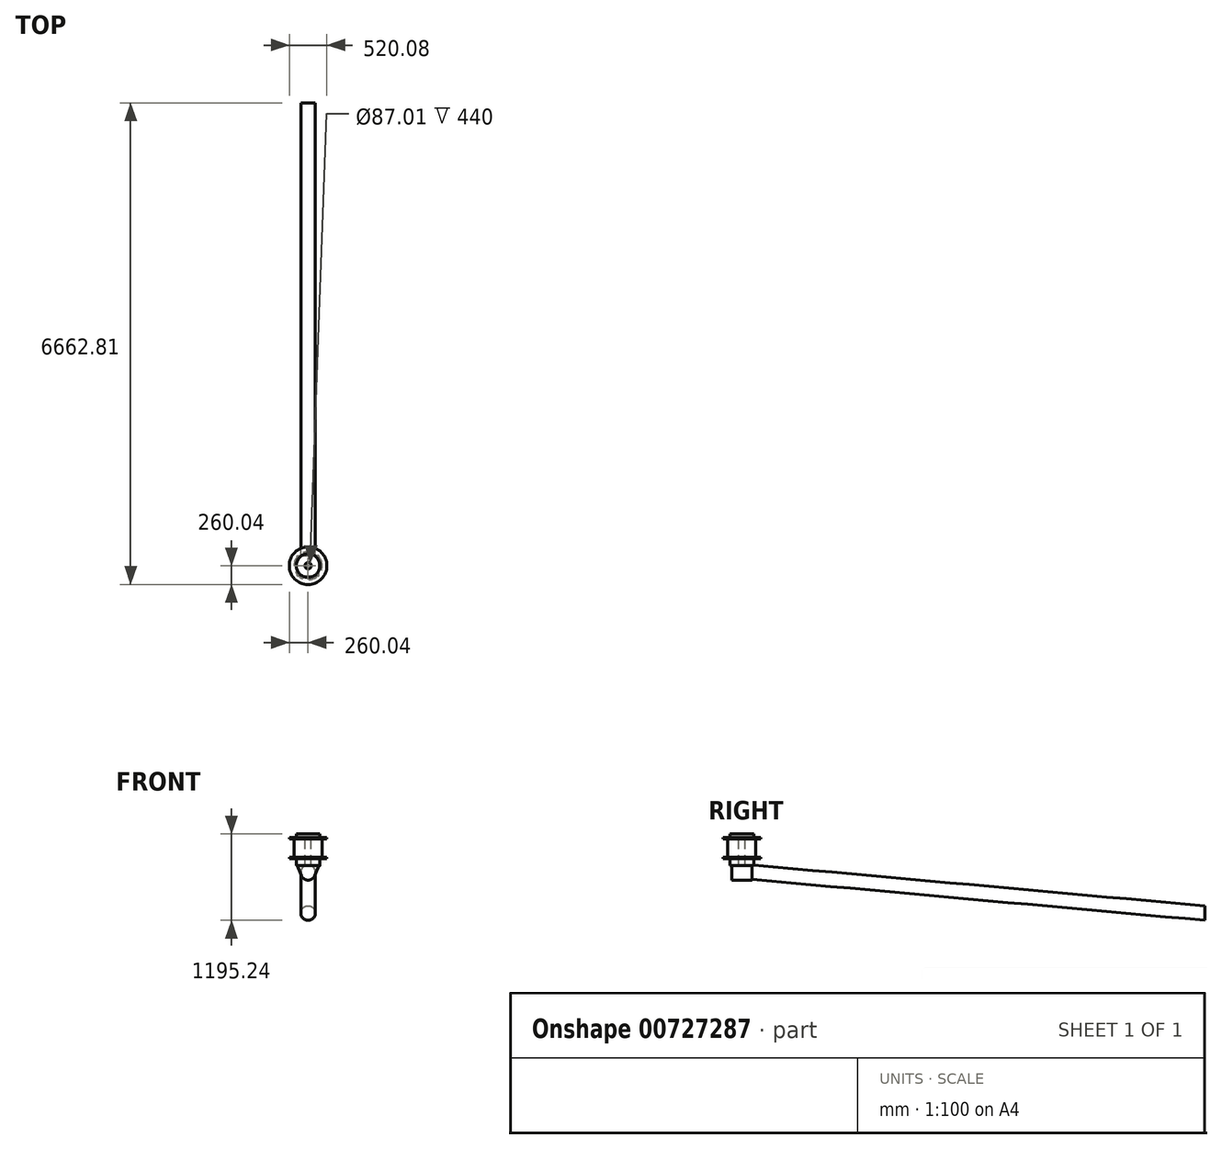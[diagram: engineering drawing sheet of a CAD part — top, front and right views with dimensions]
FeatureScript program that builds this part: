
annotation { "Feature Type Name" : "Feature", "Feature Type Description" : "" }
export const myFeature = defineFeature(function(context is Context, id is Id, definition is map)
    precondition{}
    {
        {
            var Q0;
            Q0=qCreatedBy(makeId("Front.planeOp"),FACE);
            var sketch = newSketch(context, id + "F0", { "sketchPlane" : qUnion([Q0])});
            skLineSegment(sketch, "E0", {"start": v(0, 326.34) * mm, "end": v(0, -233.1) * mm, "construction": true});
            skLineSegment(sketch, "E1", {"start": v(-43.5, 342.85) * mm, "end": v(-163.5, 342.85) * mm});
            skLineSegment(sketch, "E2", {"start": v(-163.5, 342.85) * mm, "end": v(-163.5, 292.85) * mm});
            skLineSegment(sketch, "E3", {"start": v(-163.5, 292.85) * mm, "end": v(-260.04, 292.85) * mm});
            skLineSegment(sketch, "E4", {"start": v(-260.04, 292.85) * mm, "end": v(-260.04, 272.85) * mm});
            skLineSegment(sketch, "E5", {"start": v(-260.04, 272.85) * mm, "end": v(-193.5, 272.85) * mm});
            skLineSegment(sketch, "E6", {"start": v(-193.5, 272.85) * mm, "end": v(-193.5, 22.85) * mm});
            skLineSegment(sketch, "E7", {"start": v(-193.5, 22.85) * mm, "end": v(-260.04, 22.85) * mm});
            skLineSegment(sketch, "E8", {"start": v(-260.04, 22.85) * mm, "end": v(-260.04, 2.85) * mm});
            skLineSegment(sketch, "E9", {"start": v(-260.04, 2.85) * mm, "end": v(-163.5, 2.85) * mm});
            skLineSegment(sketch, "E10", {"start": v(-163.5, 2.85) * mm, "end": v(-163.5, -97.15) * mm});
            skLineSegment(sketch, "E11", {"start": v(-163.5, -97.15) * mm, "end": v(-43.5, -97.15) * mm});
            skLineSegment(sketch, "E12", {"start": v(-43.5, -97.15) * mm, "end": v(-43.5, 342.85) * mm});
            skSolve(sketch);
        }
        {
            var Q0;
            Q0 = qSketchRegion(id + "F0", true);
            var Q1;
            Q1=sQuery(id+"F0.wireOp",EDGE,"E0");
            revolve(context, id + "F1", {"surfaceOperationType" : NewSurfaceOperationType.NEW, "entities" : qUnion([Q0]), "axis" : qUnion([Q1]), "revolveType" : RevolveType.FULL});
        }
        {
            var Q0;
            Q0=qCreatedBy(makeId("Front.planeOp"),FACE);
            var sketch = newSketch(context, id + "F2", { "sketchPlane" : qUnion([Q0])});
            skArc(sketch, "E13", {"start": v(-93.15, -233.51) * mm, "mid": v(0, -297.15) * mm, "end": v(93.15, -233.51) * mm});
            skLineSegment(sketch, "E14", {"start": v(-146.38, -97.15) * mm, "end": v(-93.15, -233.51) * mm});
            skLineSegment(sketch, "E15", {"start": v(146.38, -97.15) * mm, "end": v(93.15, -233.51) * mm});
            skLineSegment(sketch, "E16", {"start": v(-146.38, -97.15) * mm, "end": v(146.38, -97.15) * mm});
            skSolve(sketch);
        }
        {
            var Q0;
            Q0 = qSketchRegion(id + "F2", true);
            extrude(context, id + "F3", {"entities" : qUnion([Q0]), "operationType" : NewBodyOperationType.ADD, "endBound" : BoundingType.SYMMETRIC, "depth" : 277.37 * mm, "offsetDistance" : 25.4 * mm});
        }
        {
            var Q0;
            Q0=qCreatedBy(makeId("Right.planeOp"),FACE);
            cPlane(context, id + "F4", {"entities" : qUnion([Q0]), "cplaneType" : CPlaneType.OFFSET, "offset" : 0 * mm, "width" : 152.4 * mm, "height" : 152.4 * mm});
        }
        {
            var Q0;
            Q0=qCreatedBy(id+"F4.planeOp",FACE);
            var sketch = newSketch(context, id + "F5", { "sketchPlane" : qUnion([Q0])});
            skLineSegment(sketch, "E17", {"start": v(176.04, -185.3) * mm, "end": v(6440.13, -752.39) * mm});
            skSolve(sketch);
        }
        {
            var Q0;
            Q0=makeQuery(id+"F3.opExtrude","CAP_FACE",FACE,{"disambiguationData":[OSD([sQuery(id+"F2.wireOp",EDGE,"E13"),sQuery(id+"F2.wireOp",EDGE,"E14"),sQuery(id+"F2.wireOp",EDGE,"E15"),sQuery(id+"F2.wireOp",EDGE,"E16")])],"isStart":true});
            var sketch = newSketch(context, id + "F6", { "sketchPlane" : qUnion([Q0])});
            skCircle(sketch, "E18", {"center": v(0, -185.3) * mm, "radius": 100 * mm});
            skSolve(sketch);
        }
        {
            var Q0;
            Q0=makeQuery(id+"F6.imprint","IMPRINT",FACE,{"disambiguationData":[TD([[makeQuery(id+"F6.imprint","IMPRINT",EDGE,{"derivedFrom":sQuery(id+"F6.wireOp",EDGE,"E18")}),1.0]])]});
            var Q1;
            Q1=sQuery(id+"F5.wireOp",EDGE,"E17");
            sweep(context, id + "F7", {"operationType" : NewBodyOperationType.ADD, "profiles" : qUnion([Q0]), "path" : qUnion([Q1])});
        }
    });
